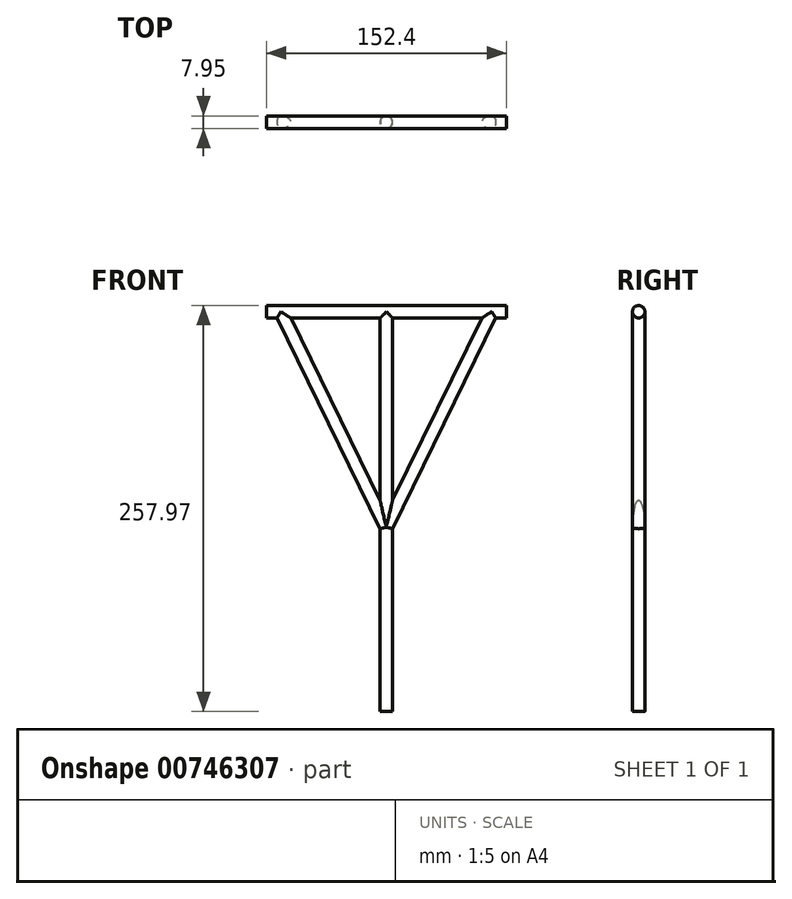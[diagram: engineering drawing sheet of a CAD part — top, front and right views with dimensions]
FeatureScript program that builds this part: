
annotation { "Feature Type Name" : "Feature", "Feature Type Description" : "" }
export const myFeature = defineFeature(function(context is Context, id is Id, definition is map)
    precondition{}
    {
        {
            var Q0;
            Q0=qCreatedBy(makeId("Front.planeOp"),FACE);
            var sketch = newSketch(context, id + "F0", { "sketchPlane" : qUnion([Q0])});
            skLineSegment(sketch, "E0", {"start": v(-76, 227.05) * mm, "end": v(76.4, 227.05) * mm});
            skLineSegment(sketch, "E1", {"start": v(0.2, 227.05) * mm, "end": v(0, -26.95) * mm});
            skLineSegment(sketch, "E2", {"start": v(-66.9, 227.05) * mm, "end": v(0.1, 90.16) * mm});
            skLineSegment(sketch, "E3", {"start": v(0.1, 90.16) * mm, "end": v(67.08, 227.05) * mm});
            skSolve(sketch);
        }
        {
            var Q0;
            Q0 = qSketchRegion(id + "F0", true);
            var Q1;
            Q1=sQuery(id+"F0.wireOp",EDGE,"E3");
            extrude(context, id + "F1", {"entities" : qUnion([Q0]), "bodyType" : ToolBodyType.SURFACE, "surfaceEntities" : qUnion([Q1]), "depth" : 3.98 * mm, "offsetDistance" : 25.4 * mm});
        }
        {
            var Q0;
            Q0=sQuery(id+"F0.wireOp",EDGE,"E2");
            extrude(context, id + "F2", {"bodyType" : ToolBodyType.SURFACE, "surfaceEntities" : qUnion([Q0]), "depth" : 3.98 * mm, "offsetDistance" : 25.4 * mm});
        }
        {
            var Q0;
            Q0=sQuery(id+"F0.wireOp",EDGE,"E0");
            extrude(context, id + "F3", {"bodyType" : ToolBodyType.SURFACE, "surfaceEntities" : qUnion([Q0]), "depth" : 3.98 * mm, "offsetDistance" : 25.4 * mm});
        }
        {
            var Q0;
            Q0=sQuery(id+"F0.wireOp",EDGE,"E1");
            extrude(context, id + "F4", {"bodyType" : ToolBodyType.SURFACE, "surfaceEntities" : qUnion([Q0]), "depth" : 3.98 * mm, "offsetDistance" : 25.4 * mm});
        }
        {
            var Q0;
            Q0=makeQuery(id+"F4.opExtrude","SWEPT_FACE",FACE,{"disambiguationData":[OSD([sQuery(id+"F0.wireOp",EDGE,"E1")])]});
            var Q1;
            Q1=makeQuery(id+"F4.opExtrude","CAP_EDGE",EDGE,{"disambiguationData":[OSD([sQuery(id+"F0.wireOp",EDGE,"E1")])],"isStart":false});
            revolve(context, id + "F5", {"surfaceOperationType" : NewSurfaceOperationType.NEW, "entities" : qUnion([Q0]), "axis" : qUnion([Q1]), "revolveType" : RevolveType.FULL});
        }
        {
            var Q0;
            Q0=makeQuery(id+"F3.opExtrude","SWEPT_FACE",FACE,{"disambiguationData":[OSD([sQuery(id+"F0.wireOp",EDGE,"E0")])]});
            var Q1;
            Q1=makeQuery(id+"F3.opExtrude","CAP_EDGE",EDGE,{"disambiguationData":[OSD([sQuery(id+"F0.wireOp",EDGE,"E0")])],"isStart":false});
            revolve(context, id + "F6", {"operationType" : NewBodyOperationType.ADD, "surfaceOperationType" : NewSurfaceOperationType.NEW, "entities" : qUnion([Q0]), "axis" : qUnion([Q1]), "revolveType" : RevolveType.FULL});
        }
        {
            var Q0;
            Q0=makeQuery(id+"F2.opExtrude","SWEPT_FACE",FACE,{"disambiguationData":[OSD([sQuery(id+"F0.wireOp",EDGE,"E2")])]});
            var Q1;
            Q1=makeQuery(id+"F2.opExtrude","CAP_EDGE",EDGE,{"disambiguationData":[OSD([sQuery(id+"F0.wireOp",EDGE,"E2")])],"isStart":false});
            revolve(context, id + "F7", {"operationType" : NewBodyOperationType.ADD, "surfaceOperationType" : NewSurfaceOperationType.NEW, "entities" : qUnion([Q0]), "axis" : qUnion([Q1]), "revolveType" : RevolveType.FULL});
        }
        {
            var Q0;
            Q0=makeQuery(id+"F1.opExtrude","SWEPT_FACE",FACE,{"disambiguationData":[OSD([sQuery(id+"F0.wireOp",EDGE,"E3")])]});
            var Q1;
            Q1=makeQuery(id+"F1.opExtrude","CAP_EDGE",EDGE,{"disambiguationData":[OSD([sQuery(id+"F0.wireOp",EDGE,"E3")])],"isStart":false});
            revolve(context, id + "F8", {"operationType" : NewBodyOperationType.ADD, "surfaceOperationType" : NewSurfaceOperationType.NEW, "entities" : qUnion([Q0]), "axis" : qUnion([Q1]), "revolveType" : RevolveType.FULL});
        }
    });
